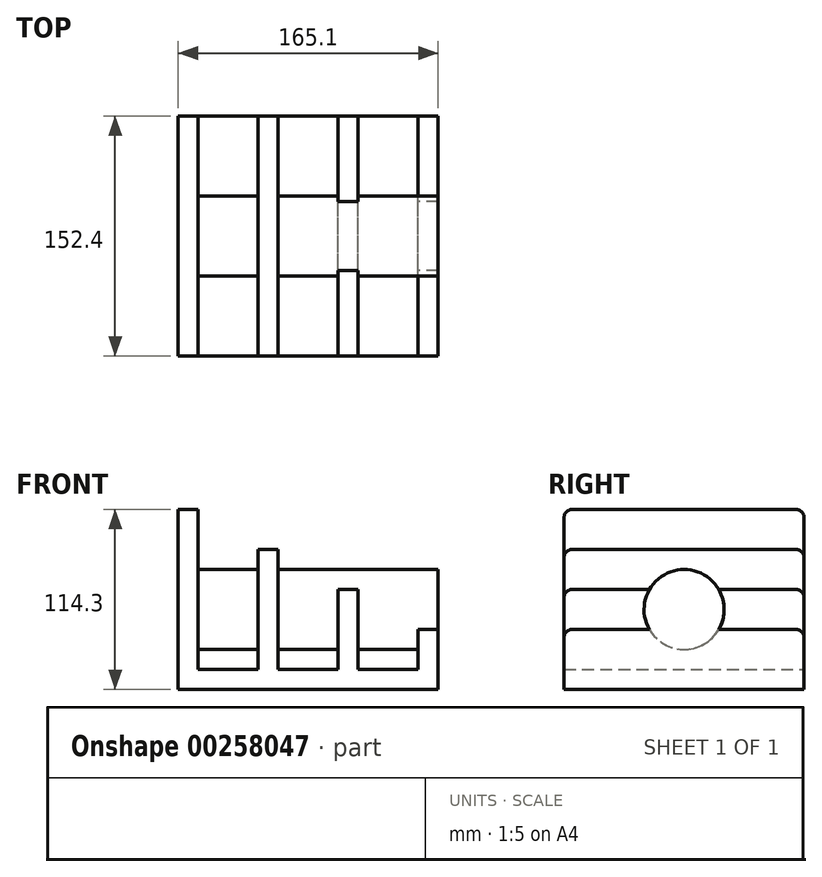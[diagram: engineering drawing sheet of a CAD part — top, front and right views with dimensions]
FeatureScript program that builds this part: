
annotation { "Feature Type Name" : "Feature", "Feature Type Description" : "" }
export const myFeature = defineFeature(function(context is Context, id is Id, definition is map)
    precondition{}
    {
        {
            var Q0;
            Q0=qCreatedBy(makeId("Front.planeOp"),FACE);
            var sketch = newSketch(context, id + "F0", { "sketchPlane" : qUnion([Q0])});
            skLineSegment(sketch, "E0", {"start": v(-63.5, 93.86) * mm, "end": v(-63.5, -20.44) * mm});
            skLineSegment(sketch, "E1", {"start": v(-63.5, -20.44) * mm, "end": v(101.6, -20.44) * mm});
            skLineSegment(sketch, "E2", {"start": v(101.6, -20.44) * mm, "end": v(101.6, 17.66) * mm});
            skLineSegment(sketch, "E3", {"start": v(101.6, 17.66) * mm, "end": v(88.9, 17.66) * mm});
            skLineSegment(sketch, "E4", {"start": v(88.9, 17.66) * mm, "end": v(88.9, -7.74) * mm});
            skLineSegment(sketch, "E5", {"start": v(88.9, -7.74) * mm, "end": v(32.96, -7.74) * mm});
            skLineSegment(sketch, "E6", {"start": v(38.1, 43.06) * mm, "end": v(38.1, -7.74) * mm});
            skLineSegment(sketch, "E7", {"start": v(38.1, -7.74) * mm, "end": v(-12.7, -7.74) * mm});
            skLineSegment(sketch, "E8", {"start": v(-12.7, -7.74) * mm, "end": v(-12.7, 68.46) * mm});
            skLineSegment(sketch, "E9", {"start": v(0, 68.46) * mm, "end": v(-12.7, 68.46) * mm});
            skLineSegment(sketch, "E10", {"start": v(0, 68.46) * mm, "end": v(0, -7.74) * mm});
            skLineSegment(sketch, "E11", {"start": v(0, -7.74) * mm, "end": v(-50.8, -7.74) * mm});
            skLineSegment(sketch, "E12", {"start": v(-50.8, -7.74) * mm, "end": v(-50.8, 93.86) * mm});
            skLineSegment(sketch, "E13", {"start": v(-50.8, 93.86) * mm, "end": v(-63.5, 93.86) * mm});
            skLineSegment(sketch, "E14", {"start": v(38.1, 43.06) * mm, "end": v(50.8, 43.06) * mm});
            skLineSegment(sketch, "E15", {"start": v(50.8, 43.06) * mm, "end": v(50.8, -7.74) * mm});
            skSolve(sketch);
        }
        {
            var Q0;
            Q0 = qSketchRegion(id + "F0", true);
            extrude(context, id + "F1", {"entities" : qUnion([Q0]), "depth" : 152.4 * mm});
        }
        {
            var Q0;
            Q0=makeQuery(id+"F1.opExtrude","SWEPT_FACE",FACE,{"disambiguationData":[OSD([sQuery(id+"F0.wireOp",EDGE,"E0")])]});
            var sketch = newSketch(context, id + "F2", { "sketchPlane" : qUnion([Q0])});
            skCircle(sketch, "E16", {"center": v(76.2, 30.36) * mm, "radius": 25.4 * mm});
            skSolve(sketch);
        }
        {
            var Q0;
            Q0 = qSketchRegion(id + "F2", true);
            extrude(context, id + "F3", {"entities" : qUnion([Q0]), "operationType" : NewBodyOperationType.ADD, "oppositeDirection" : true, "depth" : 165.1 * mm});
        }
        {
            var Q0;
            Q0=makeQuery(id+"F1.opExtrude","CAP_EDGE",EDGE,{"disambiguationData":[OSD([sQuery(id+"F0.wireOp",EDGE,"E13")])],"isStart":false});
            var Q1;
            Q1=makeQuery(id+"F1.opExtrude","CAP_EDGE",EDGE,{"disambiguationData":[OSD([sQuery(id+"F0.wireOp",EDGE,"E13")])],"isStart":true});
            var Q2;
            Q2=makeQuery(id+"F1.opExtrude","CAP_EDGE",EDGE,{"disambiguationData":[OSD([sQuery(id+"F0.wireOp",EDGE,"E9")])],"isStart":false});
            var Q3;
            Q3=makeQuery(id+"F1.opExtrude","CAP_EDGE",EDGE,{"disambiguationData":[OSD([sQuery(id+"F0.wireOp",EDGE,"E9")])],"isStart":true});
            var Q4;
            Q4=makeQuery(id+"F1.opExtrude","CAP_EDGE",EDGE,{"disambiguationData":[OSD([sQuery(id+"F0.wireOp",EDGE,"E14")])],"isStart":true});
            var Q5;
            Q5=makeQuery(id+"F1.opExtrude","CAP_EDGE",EDGE,{"disambiguationData":[OSD([sQuery(id+"F0.wireOp",EDGE,"E14")])],"isStart":false});
            var Q6;
            Q6=makeQuery(id+"F1.opExtrude","CAP_EDGE",EDGE,{"disambiguationData":[OSD([sQuery(id+"F0.wireOp",EDGE,"E3")])],"isStart":false});
            var Q7;
            Q7=makeQuery(id+"F1.opExtrude","CAP_EDGE",EDGE,{"disambiguationData":[OSD([sQuery(id+"F0.wireOp",EDGE,"E3")])],"isStart":true});
            fillet(context, id + "F4", {"entities" : qUnion([Q0, Q1, Q2, Q3, Q4, Q5, Q6, Q7]), "radius" : 5.08 * mm, "tangentPropagation" : true, "allowEdgeOverflow" : false});
        }
    });
